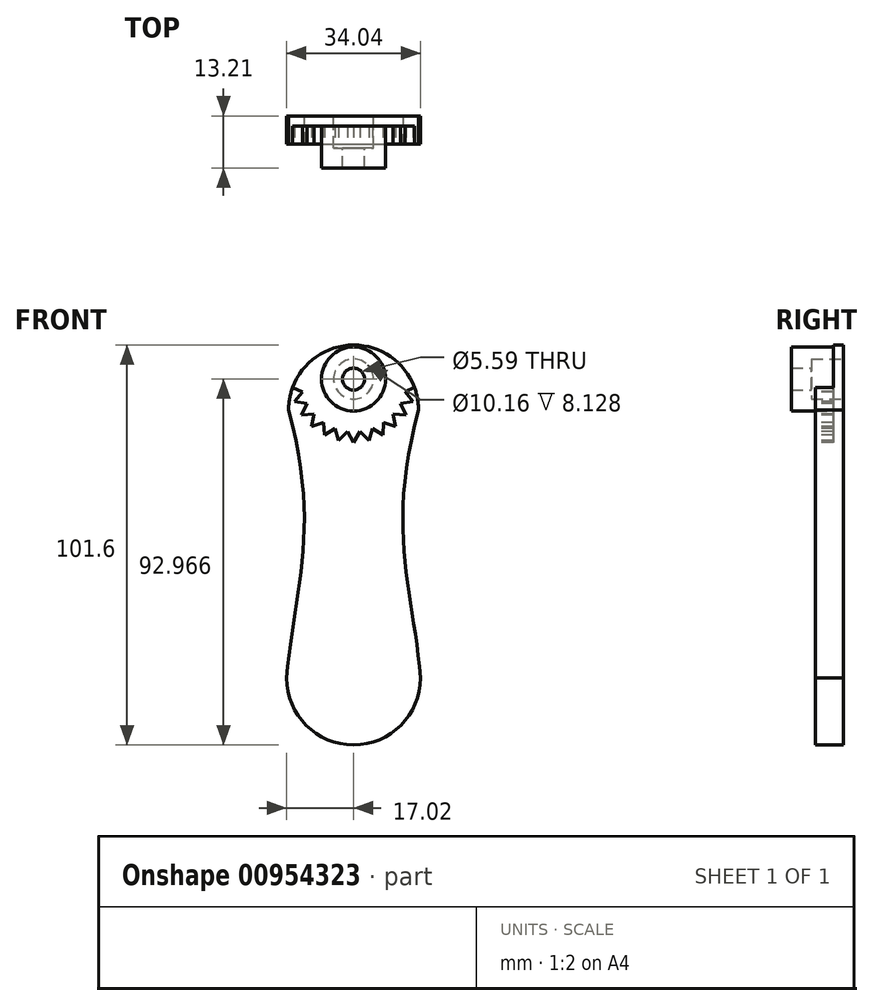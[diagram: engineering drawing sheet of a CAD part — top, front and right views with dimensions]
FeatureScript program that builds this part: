
annotation { "Feature Type Name" : "Feature", "Feature Type Description" : "" }
export const myFeature = defineFeature(function(context is Context, id is Id, definition is map)
    precondition{}
    {
        {
            var Q0;
            Q0=qCreatedBy(makeId("Front.planeOp"),FACE);
            var sketch = newSketch(context, id + "F0", { "sketchPlane" : qUnion([Q0])});
            skArc(sketch, "E0", {"start": v(16.51, 16.2) * mm, "mid": v(0, 32.71) * mm, "end": v(-16.51, 16.2) * mm});
            skArc(sketch, "E1", {"start": v(-17.02, -51.87) * mm, "mid": v(0, -68.89) * mm, "end": v(17.02, -51.87) * mm});
            skPoint(sketch, "E2", {"position": v(0, 32.71) * mm});
            skPoint(sketch, "E3", {"position": v(0, -68.89) * mm});
            skFitSpline(sketch, "E4", {"points": [v(-16.51, 16.2) * mm, v(-17.02, -51.87) * mm], "startDerivative": vector(24.94, -92.74) * mm, "endDerivative": vector(-5.66, -67.8) * mm});
            skFitSpline(sketch, "E5.MirrorCS", {"points": [v(16.51, 16.2) * mm, v(17.02, -51.87) * mm], "startDerivative": vector(-24.94, -92.74) * mm, "endDerivative": vector(5.66, -67.8) * mm});
            skLineSegment(sketch, "E6", {"start": v(-12.7, -17.82) * mm, "end": v(12.7, -17.82) * mm, "construction": true});
            skSolve(sketch);
        }
        {
            var Q0;
            Q0=makeQuery(id+"F0.imprint","IMPRINT",FACE,{"disambiguationData":[TD([[makeQuery(id+"F0.imprint","IMPRINT",EDGE,{"derivedFrom":sQuery(id+"F0.wireOp",EDGE,"E0")}),1.0]])]});
            extrude(context, id + "F1", {"entities" : qUnion([Q0]), "depth" : 7.11 * mm, "offsetDistance" : 25.4 * mm});
        }
        {
            var Q0;
            Q0=makeQuery(id+"F1.opExtrude","CAP_FACE",FACE,{"disambiguationData":[OSD([sQuery(id+"F0.wireOp",EDGE,"E0"),sQuery(id+"F0.wireOp",EDGE,"E1"),sQuery(id+"F0.wireOp",EDGE,"E4"),sQuery(id+"F0.wireOp",EDGE,"E5.MirrorCS")])],"isStart":false});
            var sketch = newSketch(context, id + "F2", { "sketchPlane" : qUnion([Q0])});
            skLineSegment(sketch, "E7", {"start": v(0, 32.71) * mm, "end": v(0, 24.08) * mm, "construction": true});
            skCircle(sketch, "E8", {"center": v(0, 24.08) * mm, "radius": 2.8 * mm});
            skCircle(sketch, "E9", {"center": v(0, 24.08) * mm, "radius": 8.13 * mm});
            skSolve(sketch);
        }
        {
            var Q0;
            Q0=makeQuery(id+"F2.imprint","IMPRINT",FACE,{"disambiguationData":[TD([[makeQuery(id+"F2.imprint","IMPRINT",EDGE,{"derivedFrom":sQuery(id+"F2.wireOp",EDGE,"E8")}),-1.0]])]});
            extrude(context, id + "F3", {"entities" : qUnion([Q0]), "operationType" : NewBodyOperationType.ADD, "depth" : 6.1 * mm, "offsetDistance" : 25.4 * mm});
        }
        {
            var Q0;
            Q0=makeQuery(id+"F3.boolean.opBoolean","SPLIT",FACE,{"disambiguationData":[TD([makeQuery(id+"F3.opExtrude","SWEPT_FACE",FACE,{"disambiguationData":[OSD([sQuery(id+"F2.wireOp",EDGE,"E8")])]})])],"derivedFrom":makeQuery(id+"F1.opExtrude","CAP_FACE",FACE,{"disambiguationData":[OSD([sQuery(id+"F0.wireOp",EDGE,"E0"),sQuery(id+"F0.wireOp",EDGE,"E1"),sQuery(id+"F0.wireOp",EDGE,"E4"),sQuery(id+"F0.wireOp",EDGE,"E5.MirrorCS")])],"isStart":false})});
            extrude(context, id + "F4", {"entities" : qUnion([Q0]), "operationType" : NewBodyOperationType.REMOVE, "endBound" : BoundingType.SYMMETRIC, "oppositeDirection" : true, "depth" : 101.6 * mm, "offsetDistance" : 25.4 * mm});
        }
        {
            var Q0;
            {var subQ0=sQuery(id+"F0.wireOp",EDGE,"E4");var subQ1=sQuery(id+"F0.wireOp",EDGE,"E1");var subQ2=sQuery(id+"F0.wireOp",EDGE,"E5.MirrorCS");var subQ3=sQuery(id+"F0.wireOp",EDGE,"E0");Q0=makeQuery(id+"F3.boolean.opBoolean","SPLIT",FACE,{"disambiguationData":[TD([makeQuery(id+"F1.opExtrude","SWEPT_FACE",FACE,{"disambiguationData":[OSD([subQ3])]})])],"derivedFrom":makeQuery(id+"F1.opExtrude","CAP_FACE",FACE,{"disambiguationData":[OSD([subQ3,subQ1,subQ0,subQ2])],"isStart":false})});}
            var sketch = newSketch(context, id + "F5", { "sketchPlane" : qUnion([Q0])});
            skLineSegment(sketch, "E10", {"start": v(0, 24.08) * mm, "end": v(0, 0) * mm, "construction": true});
            skLineSegment(sketch, "E11", {"start": v(-15.97, 22.08) * mm, "end": v(-12.93, 20.8) * mm});
            skLineSegment(sketch, "E12.1.0", {"start": v(-12.95, 20.88) * mm, "end": v(-15.03, 18.32) * mm});
            skLineSegment(sketch, "E12.1.1", {"start": v(-15.03, 18.32) * mm, "end": v(-11.77, 17.8) * mm});
            skLineSegment(sketch, "E12.2.0", {"start": v(-11.8, 17.88) * mm, "end": v(-13.21, 14.9) * mm});
            skLineSegment(sketch, "E12.2.1", {"start": v(-13.21, 14.9) * mm, "end": v(-9.92, 15.17) * mm});
            skLineSegment(sketch, "E12.3.0", {"start": v(-9.98, 15.23) * mm, "end": v(-10.63, 12) * mm});
            skLineSegment(sketch, "E12.3.1", {"start": v(-10.63, 12) * mm, "end": v(-7.5, 13.05) * mm});
            skLineSegment(sketch, "E12.4.0", {"start": v(-7.58, 13.1) * mm, "end": v(-7.43, 9.8) * mm});
            skLineSegment(sketch, "E12.4.1", {"start": v(-7.43, 9.8) * mm, "end": v(-4.65, 11.58) * mm});
            skLineSegment(sketch, "E12.5.0", {"start": v(-4.73, 11.6) * mm, "end": v(-3.8, 8.44) * mm});
            skLineSegment(sketch, "E12.5.1", {"start": v(-3.8, 8.44) * mm, "end": v(-1.52, 10.83) * mm});
            skLineSegment(sketch, "E12.6.0", {"start": v(-1.6, 10.84) * mm, "end": v(0.05, 7.98) * mm});
            skLineSegment(sketch, "E12.6.1", {"start": v(0.05, 7.98) * mm, "end": v(1.7, 10.85) * mm});
            skLineSegment(sketch, "E12.7.0", {"start": v(1.6, 10.84) * mm, "end": v(3.9, 8.46) * mm});
            skLineSegment(sketch, "E12.7.1", {"start": v(3.9, 8.46) * mm, "end": v(4.81, 11.64) * mm});
            skLineSegment(sketch, "E12.8.0", {"start": v(4.73, 11.6) * mm, "end": v(7.53, 9.85) * mm});
            skLineSegment(sketch, "E12.8.1", {"start": v(7.53, 9.85) * mm, "end": v(7.65, 13.15) * mm});
            skLineSegment(sketch, "E12.9.0", {"start": v(7.58, 13.1) * mm, "end": v(10.71, 12.07) * mm});
            skLineSegment(sketch, "E12.9.1", {"start": v(10.71, 12.07) * mm, "end": v(10.04, 15.3) * mm});
            skLineSegment(sketch, "E12.10.0", {"start": v(9.98, 15.23) * mm, "end": v(13.27, 14.98) * mm});
            skLineSegment(sketch, "E12.10.1", {"start": v(13.27, 14.98) * mm, "end": v(11.85, 17.96) * mm});
            skLineSegment(sketch, "E12.11.0", {"start": v(11.8, 17.88) * mm, "end": v(15.07, 18.42) * mm});
            skLineSegment(sketch, "E12.11.1", {"start": v(15.07, 18.42) * mm, "end": v(12.97, 20.97) * mm});
            skLineSegment(sketch, "E12.12.0", {"start": v(12.95, 20.88) * mm, "end": v(15.98, 22.19) * mm});
            skPoint(sketch, "E12.center", {"position": v(0, 24.08) * mm});
            skArc(sketch, "E13.trimOffspring", {"start": v(-13.33, 24.08) * mm, "mid": v(-13.33, 24.03) * mm, "end": v(-13.33, 23.99) * mm});
            skArc(sketch, "E14.trimOffspring", {"start": v(-12.95, 20.88) * mm, "mid": v(-12.94, 20.84) * mm, "end": v(-12.93, 20.8) * mm});
            skArc(sketch, "E15.trimOffspring", {"start": v(-11.8, 17.88) * mm, "mid": v(-11.79, 17.84) * mm, "end": v(-11.77, 17.8) * mm});
            skArc(sketch, "E16.trimOffspring", {"start": v(-9.98, 15.23) * mm, "mid": v(-9.95, 15.2) * mm, "end": v(-9.92, 15.17) * mm});
            skArc(sketch, "E17.trimOffspring", {"start": v(-7.58, 13.1) * mm, "mid": v(-7.54, 13.08) * mm, "end": v(-7.5, 13.05) * mm});
            skArc(sketch, "E18.trimOffspring", {"start": v(-4.73, 11.6) * mm, "mid": v(-4.69, 11.6) * mm, "end": v(-4.65, 11.58) * mm});
            skArc(sketch, "E19.trimOffspring", {"start": v(-1.6, 10.84) * mm, "mid": v(-1.56, 10.83) * mm, "end": v(-1.52, 10.83) * mm});
            skArc(sketch, "E20.trimOffspring", {"start": v(1.6, 10.84) * mm, "mid": v(1.65, 10.84) * mm, "end": v(1.7, 10.85) * mm});
            skArc(sketch, "E21.trimOffspring", {"start": v(4.73, 11.6) * mm, "mid": v(4.77, 11.62) * mm, "end": v(4.81, 11.64) * mm});
            skArc(sketch, "E22.trimOffspring", {"start": v(7.58, 13.1) * mm, "mid": v(7.61, 13.13) * mm, "end": v(7.65, 13.15) * mm});
            skArc(sketch, "E23.trimOffspring", {"start": v(11.8, 17.88) * mm, "mid": v(11.83, 17.92) * mm, "end": v(11.85, 17.96) * mm});
            skArc(sketch, "E24.trimOffspring", {"start": v(13.33, 24.08) * mm, "mid": v(13.33, 24.12) * mm, "end": v(13.33, 24.16) * mm});
            skArc(sketch, "E25.trimOffspring", {"start": v(12.95, 20.88) * mm, "mid": v(12.96, 20.93) * mm, "end": v(12.97, 20.97) * mm});
            skSolve(sketch);
        }
        {
            var Q0;
            Q0=qSketchRegion(id+"F5",true);
            var Q1;
            {var subQ49=sQuery(id+"F5.wireOp",EDGE,"E14.trimOffspring");Q1=makeQuery(id+"F5.imprint","IMPRINT",FACE,{"disambiguationData":[TD([[makeQuery(id+"F5.imprint","IMPRINT",EDGE,{"derivedFrom":subQ49}),1.0]])]});}
            extrude(context, id + "F6", {"entities" : qUnion([Q0, Q1]), "operationType" : NewBodyOperationType.REMOVE, "oppositeDirection" : true, "depth" : 4.57 * mm, "offsetDistance" : 25.4 * mm});
        }
        {
            var Q0;
            Q0=makeQuery(id+"F1.opExtrude","CAP_FACE",FACE,{"disambiguationData":[OSD([sQuery(id+"F0.wireOp",EDGE,"E0"),sQuery(id+"F0.wireOp",EDGE,"E1"),sQuery(id+"F0.wireOp",EDGE,"E4"),sQuery(id+"F0.wireOp",EDGE,"E5.MirrorCS")])],"isStart":true});
            var sketch = newSketch(context, id + "F7", { "sketchPlane" : qUnion([Q0])});
            skLineSegment(sketch, "E26", {"start": v(0, 32.71) * mm, "end": v(0, 24.08) * mm, "construction": true});
            skCircle(sketch, "E27", {"center": v(0, 24.08) * mm, "radius": 5.08 * mm});
            skSolve(sketch);
        }
        {
            var Q0;
            Q0=makeQuery(id+"F7.imprint","IMPRINT",FACE,{"disambiguationData":[TD([[makeQuery(id+"F7.imprint","IMPRINT",EDGE,{"derivedFrom":sQuery(id+"F7.wireOp",EDGE,"E27")}),1.0]])]});
            extrude(context, id + "F8", {"entities" : qUnion([Q0]), "operationType" : NewBodyOperationType.REMOVE, "oppositeDirection" : true, "depth" : 8.13 * mm, "offsetDistance" : 25.4 * mm});
        }
    });
